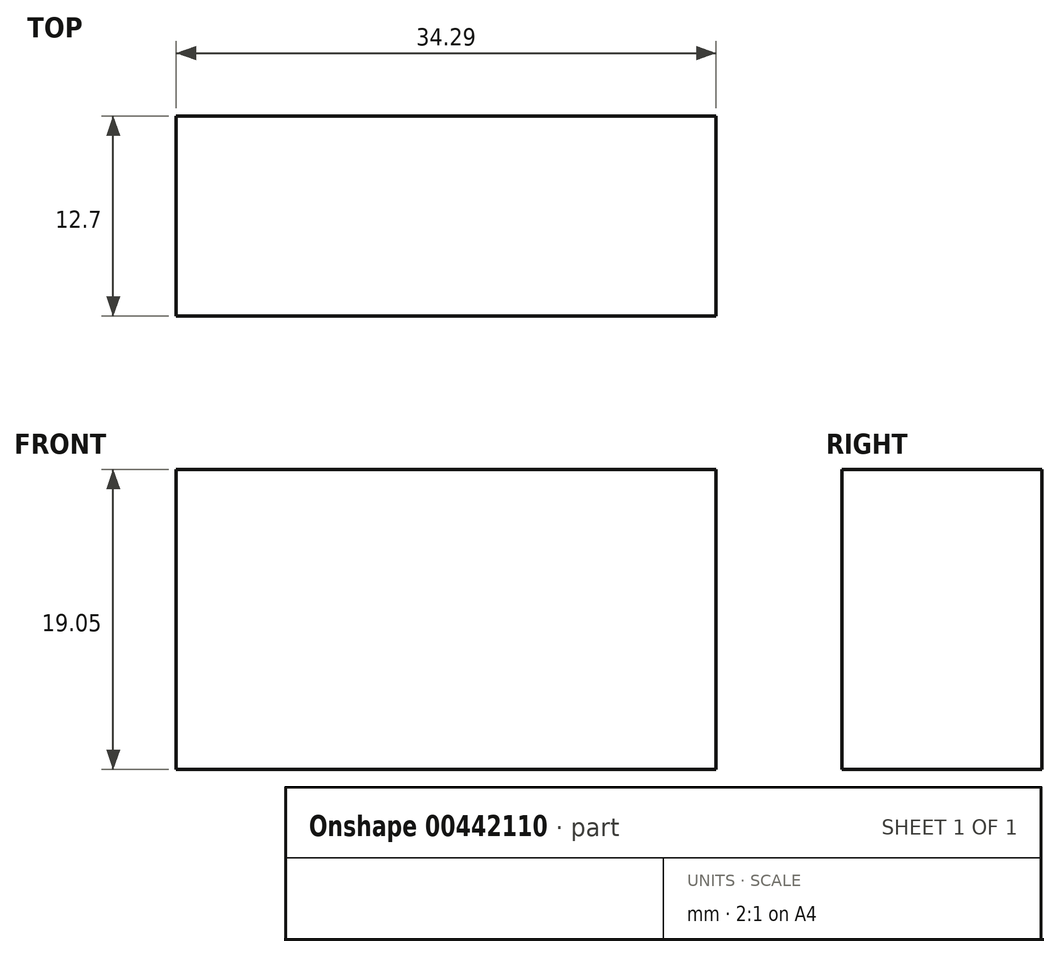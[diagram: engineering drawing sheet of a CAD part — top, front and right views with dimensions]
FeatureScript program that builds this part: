
annotation { "Feature Type Name" : "Feature", "Feature Type Description" : "" }
export const myFeature = defineFeature(function(context is Context, id is Id, definition is map)
    precondition{}
    {
        {
            var Q0;
            Q0=qCreatedBy(makeId("Front.planeOp"),FACE);
            var sketch = newSketch(context, id + "F0", { "sketchPlane" : qUnion([Q0])});
            skLineSegment(sketch, "E0.bottom", {"start": v(-15.36, 19.87) * mm, "end": v(18.93, 19.87) * mm});
            skLineSegment(sketch, "E0.top", {"start": v(-15.36, 0.82) * mm, "end": v(18.93, 0.82) * mm});
            skLineSegment(sketch, "E0.left", {"start": v(-15.36, 19.87) * mm, "end": v(-15.36, 0.82) * mm});
            skLineSegment(sketch, "E0.right", {"start": v(18.93, 19.87) * mm, "end": v(18.93, 0.82) * mm});
            skSolve(sketch);
        }
        {
            var Q0;
            Q0 = qSketchRegion(id + "F0", true);
            extrude(context, id + "F1", {"entities" : qUnion([Q0]), "depth" : 12.7 * mm});
        }
    });
